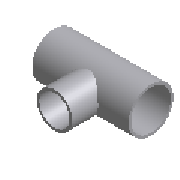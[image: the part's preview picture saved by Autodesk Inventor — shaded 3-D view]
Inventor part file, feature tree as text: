
AUTODESK INVENTOR PART (.ipt)
format: ipt  version: 2023 (Build 270158000, 158)  size: 176,640 bytes
history: native  units: mm (DEFAULTED — no unit token found)
features: other x6, extrude x4, sketch x4
ambient origin geometry x8: Origin, YZ Plane, XZ Plane, XY Plane, X Axis, Y Axis, Z Axis, Center Point
bodies: Solid1 (feature_tree)
feature tree (14):
  extrude  "Extrude1"  Depth=432.0mm
  extrude  "Extrude2"  Depth=114.3mm
  extrude  "Extrude3"  TaperAngle=0.0deg  [1 undecoded]
  extrude  "Extrude4"  Depth=216.0mm
  other  "Work Axis1"
  other  "Work Point1"
  other  "Work Axis2"
  other  "Work Point2"
  other  "Work Axis3"
  other  "Work Point3"
  sketch  "Sketch1"  dims[d0=273.0mm d1=432.0mm]
  sketch  "Sketch2"  dims[d2=0.0mm d3=114.3mm]
  sketch  "Sketch3"  dims[d4=184.0mm d5=0.0mm]
  sketch  "Sketch4"  dims[d6=260.4mm d7=216.0mm d8=0.0mm d9=107.1mm d10=216.0mm d11=0.0mm]
note: 1 required parameter value undecoded (feature->parameter linkage not recoverable at this tier; creation-order binding heuristic only, values carry confidence <= 0.55)
